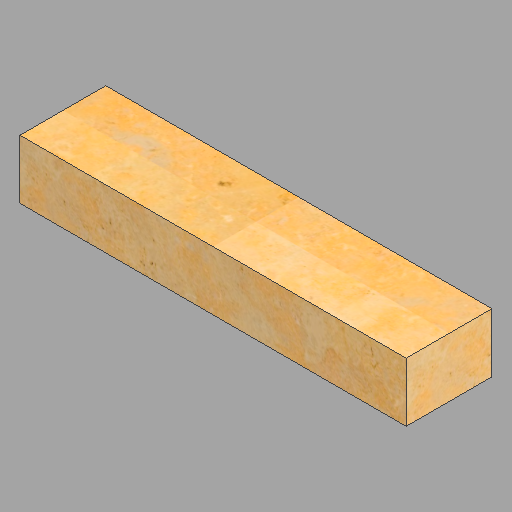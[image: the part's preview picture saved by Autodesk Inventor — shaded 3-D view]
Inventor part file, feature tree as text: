
AUTODESK INVENTOR PART (.ipt)
format: ipt  version: 2023 (Build 270158030, 158C)  size: 250,880 bytes
history: native  units: in
note: dims shown in document units (in); Inventor stores cm internally (conversion verified against a paired STEP export)
features: extrude x1, sketch x1
ambient origin geometry x8: Origin, YZ Plane, XZ Plane, XY Plane, X Axis, Y Axis, Z Axis, Center Point
bodies: Solid1 (feature_tree)
feature tree (2):
  extrude  "Extrusion1"  Depth=4.0in
  sketch  "Sketch1"  dims[d0=18.0in d1=4.0in d2=2.75in d3=0.0in]
